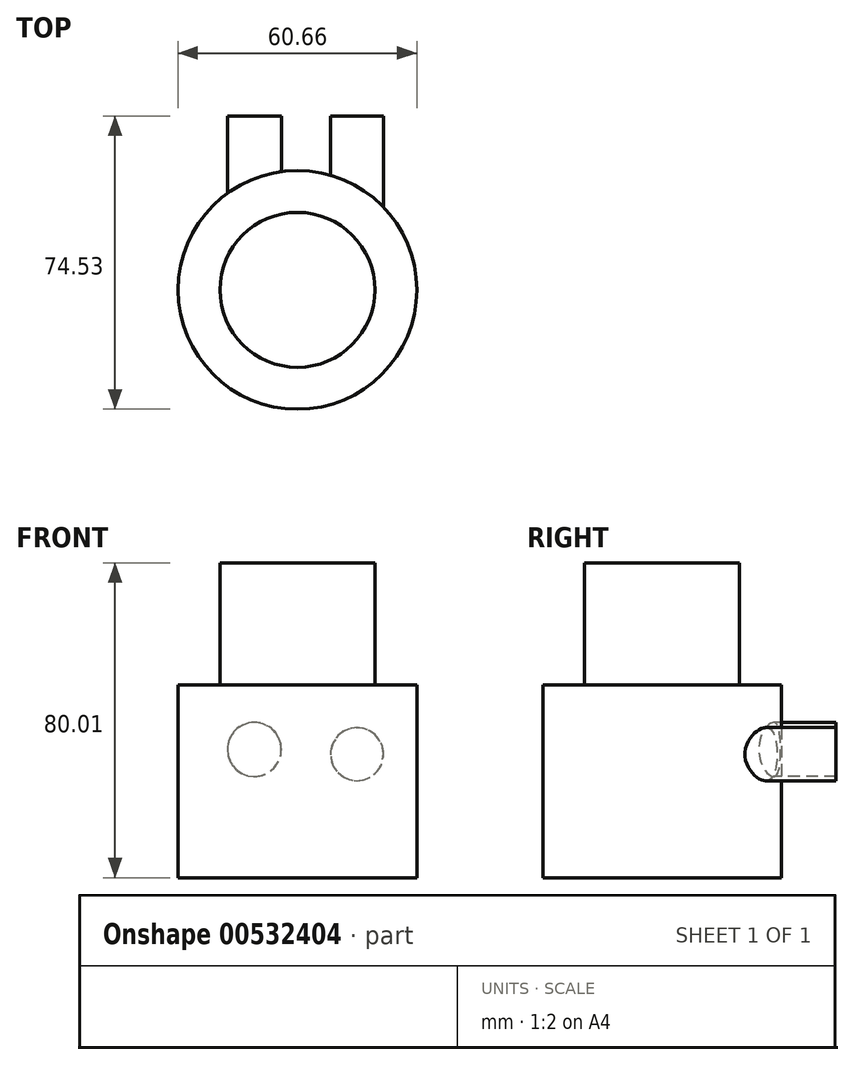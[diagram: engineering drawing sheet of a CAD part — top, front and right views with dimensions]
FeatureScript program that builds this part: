
annotation { "Feature Type Name" : "Feature", "Feature Type Description" : "" }
export const myFeature = defineFeature(function(context is Context, id is Id, definition is map)
    precondition{}
    {
        {
            var Q0;
            Q0=qCreatedBy(makeId("Top.planeOp"),FACE);
            var sketch = newSketch(context, id + "F0", { "sketchPlane" : qUnion([Q0])});
            skCircle(sketch, "E0", {"center": v(0, 0) * mm, "radius": 30.33 * mm});
            skSolve(sketch);
        }
        {
            var Q0;
            Q0 = qSketchRegion(id + "F0", true);
            extrude(context, id + "F1", {"entities" : qUnion([Q0]), "depth" : 49.02 * mm, "offsetDistance" : 25.4 * mm});
        }
        {
            var Q0;
            Q0=qCreatedBy(makeId("Top.planeOp"),FACE);
            var sketch = newSketch(context, id + "F2", { "sketchPlane" : qUnion([Q0])});
            skCircle(sketch, "E1", {"center": v(0, 0) * mm, "radius": 19.69 * mm});
            skSolve(sketch);
        }
        {
            var Q0;
            Q0=makeQuery(id+"F2.imprint","IMPRINT",FACE,{"disambiguationData":[TD([[makeQuery(id+"F2.imprint","IMPRINT",EDGE,{"derivedFrom":sQuery(id+"F2.wireOp",EDGE,"E1")}),1.0]])]});
            extrude(context, id + "F3", {"entities" : qUnion([Q0]), "operationType" : NewBodyOperationType.ADD, "depth" : 80 * mm, "offsetDistance" : 25.4 * mm});
        }
        {
            var Q0;
            Q0=qCreatedBy(makeId("Front.planeOp"),FACE);
            var sketch = newSketch(context, id + "F4", { "sketchPlane" : qUnion([Q0])});
            skCircle(sketch, "E2", {"center": v(15.13, 31.36) * mm, "radius": 6.74 * mm});
            skCircle(sketch, "E3", {"center": v(-10.95, 32.56) * mm, "radius": 6.87 * mm});
            skSolve(sketch);
        }
        {
            var Q0;
            Q0 = qSketchRegion(id + "F4", true);
            extrude(context, id + "F5", {"entities" : qUnion([Q0]), "operationType" : NewBodyOperationType.ADD, "oppositeDirection" : true, "depth" : 44.2 * mm, "offsetDistance" : 25.4 * mm});
        }
        {
            var Q0;
            Q0=makeQuery(id+"F3.opExtrude","CAP_FACE",FACE,{"disambiguationData":[OSD([sQuery(id+"F2.wireOp",EDGE,"E1")])],"isStart":false});
            extrude(context, id + "F6", {"entities" : qUnion([Q0]), "operationType" : NewBodyOperationType.ADD, "oppositeDirection" : true, "depth" : 6.6 * mm, "offsetDistance" : 25.4 * mm});
        }
    });
